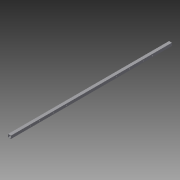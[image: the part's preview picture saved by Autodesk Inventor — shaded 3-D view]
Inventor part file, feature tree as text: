
AUTODESK INVENTOR PART (.ipt)
format: ipt  version: 2016 (Build 200138000, 138)  size: 110,592 bytes
history: native  units: in
note: dims shown in document units (in); Inventor stores cm internally (conversion verified against a paired STEP export)
features: sketch x4, reference x4, hole x2, extrude x1
ambient origin geometry x8: Origin, YZ Plane, XZ Plane, XY Plane, X Axis, Y Axis, Z Axis, Center Point
bodies: Solid1 (feature_tree)
feature tree (11):
  extrude  "Extrusion1"  Depth=1.0in
  sketch  "Sketch2"  dims[d2=0.12in d3=56.0in]
  hole  "Hole1"  [1 undecoded]
  hole  "Hole2"  [1 undecoded]
  sketch  "Sketch1"  dims[d0=1.0in d1=1.0in]
  sketch  "Sketch3"  dims[d4=0.0in d5=4.5in]
  reference  "Reference1"
  reference  "Reference2"
  reference  "Reference3"
  reference  "Reference4"
  sketch  "Sketch4"  dims[d6=4.75in d7=4.75in d8=4.5in d9=0.2656in d10=0.75in d11=0.375in d12=0.25in d13=0.5635in d14=0.125in d15=0.8108in d16=0.5in d17=0.75in d18=0.375in d19=0.25in d20=0.5635in d21=0.125in d22=0.8108in]
note: 2 required parameter values undecoded (feature->parameter linkage not recoverable at this tier; creation-order binding heuristic only, values carry confidence <= 0.55)
